# Revit family: WorkStation_Bridge_Gorbel_Steel-Track-Alum-Bridge
name_source: partatom
category: Specialty Equipment
units: mm (PartAtom-declared; Revit-internal decimal feet)

## family parameters
Always vertical = No
Classification Number = 23.50.30.37.11.14
Cut with Voids When Loaded = No
Enable Cutting in Views = No
Maintain Annotation Orientation = No
Part Type = Normal
Room Calculation Point = No
Round Connector Dimension = Use Diameter
Shared = No
Work Plane-Based = Yes

## types (1)
- WorkStation_Bridge_Gorbel_Steel-Track-Alum-Bridge
    Array = 5
    Assembly Code = D1090300
    Body Material = Aluminium
    Capacity (Lbs) = 0.00 kip
    D = 0' - 3"
    D+6 = 0' - 9"
    Default Elevation = 4' - 0"
    Description = Gorbel
    Expected Lifespan (Years) = 0
    Fixture Material = Steel
    Installation-Fabrication = https://www.gorbel.com
    Keynote = 14600
    L = 15' - 0"
    L1 = 15' - 0"
    L4 = 12' - 0"
    L5 = 1' - 6"
    L6 = 0' - 7"
    L7 = 1' - 0"
    L8 = 10' - 0"
    L9 = 1' - 0"
    Maintenance Schedule (Months) = 0
    Manufacturer = Gorbel Inc
    Manufacturer Fax = 800-828-1808;585-924-6273
    Manufacturer Website = https://www.gorbel.com
    Model = As Specified
    OAH = 11' - 0 1/4"
    OAW = 16' - 4"
    Product Data = http://arcat.com
    Product Properties = https://www.gorbel.com
    Revision = R1_05-2011
    Runway Length = 60' - 0"
    Sales Information = https://www.gorbel.com
    Send Message = http://www.arcat.com
    Specification = http://www.arcat.com
    Test Data = https://www.gorbel.com
    URL = https://www.gorbel.com
    Warranty Duration (Years) = 0

## geometry (parser evidence)
native form markers: Sweep x17
no freeform markers — native parametric forms only
